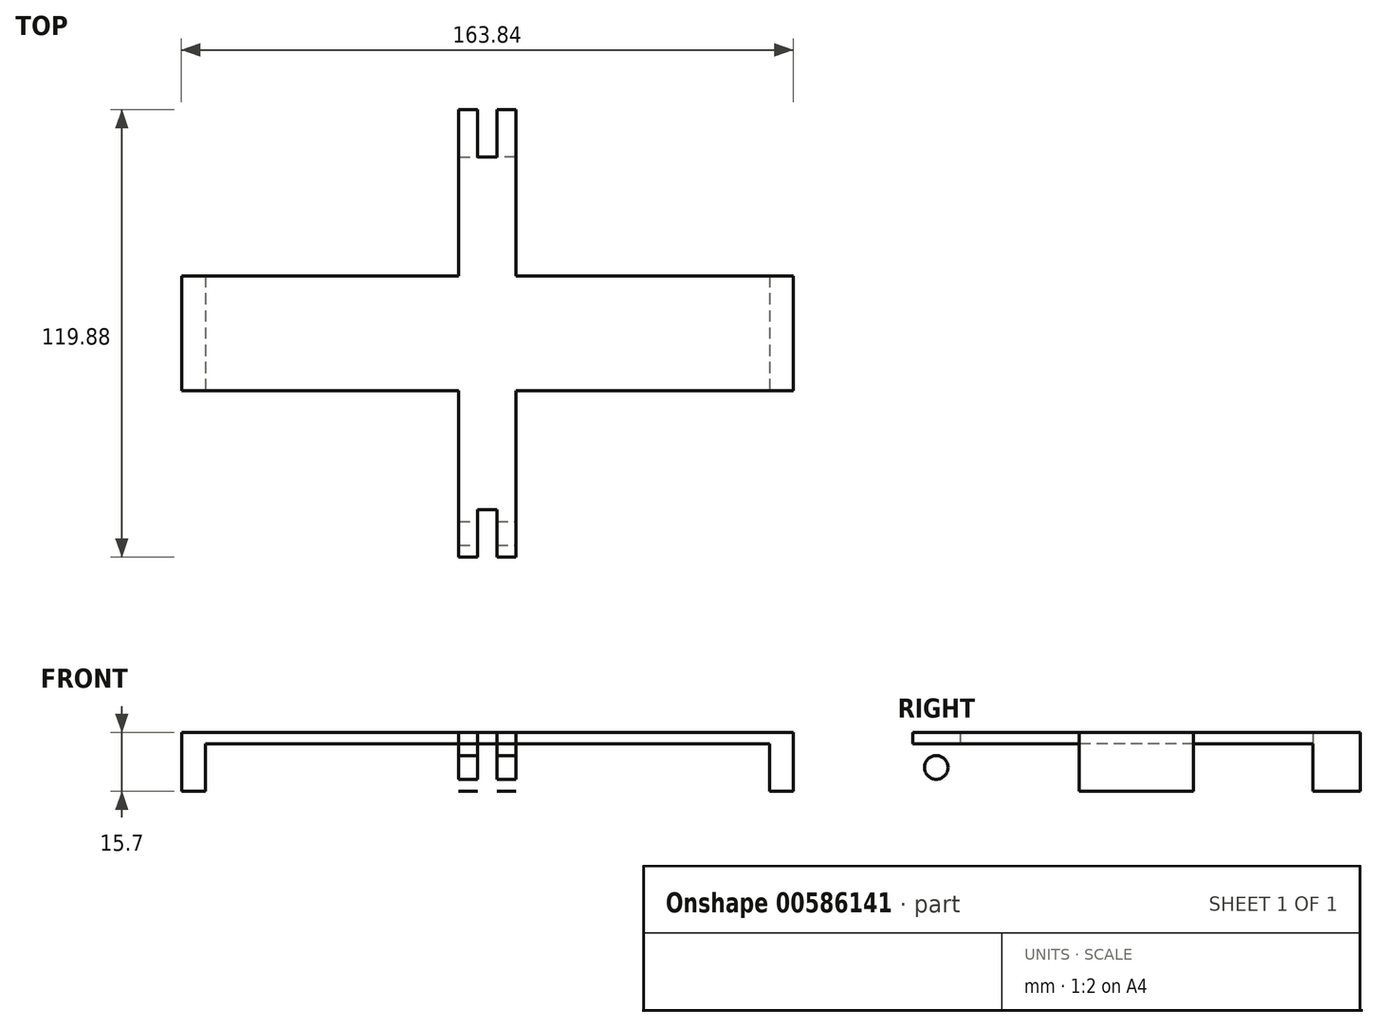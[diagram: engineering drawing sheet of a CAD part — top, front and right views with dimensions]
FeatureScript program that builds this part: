
annotation { "Feature Type Name" : "Feature", "Feature Type Description" : "" }
export const myFeature = defineFeature(function(context is Context, id is Id, definition is map)
    precondition{}
    {
        {
            var Q0;
            Q0=qCreatedBy(makeId("Top.planeOp"),FACE);
            var sketch = newSketch(context, id + "F0", { "sketchPlane" : qUnion([Q0])});
            skLineSegment(sketch, "E0.bottom", {"start": v(-7.62, 59.94) * mm, "end": v(7.62, 59.94) * mm});
            skLineSegment(sketch, "E0.top", {"start": v(-7.62, -59.94) * mm, "end": v(7.62, -59.94) * mm});
            skLineSegment(sketch, "E0.left", {"start": v(-7.62, 59.94) * mm, "end": v(-7.62, 15.36) * mm});
            skLineSegment(sketch, "E0.right", {"start": v(7.62, 59.94) * mm, "end": v(7.62, 15.36) * mm});
            skPoint(sketch, "E0.middle", {"position": v(0, 0) * mm});
            skLineSegment(sketch, "E1.bottom", {"start": v(81.92, 15.36) * mm, "end": v(7.62, 15.36) * mm});
            skLineSegment(sketch, "E1.top", {"start": v(81.92, -15.36) * mm, "end": v(7.62, -15.36) * mm});
            skLineSegment(sketch, "E1.left", {"start": v(81.92, 15.36) * mm, "end": v(81.92, -15.36) * mm});
            skLineSegment(sketch, "E1.right", {"start": v(-81.92, 15.36) * mm, "end": v(-81.92, -15.36) * mm});
            skLineSegment(sketch, "E2.trimOffspring", {"start": v(-7.62, 15.36) * mm, "end": v(-81.92, 15.36) * mm});
            skLineSegment(sketch, "E3.trimOffspring", {"start": v(-7.62, -15.36) * mm, "end": v(-7.62, -59.94) * mm});
            skLineSegment(sketch, "E4.trimOffspring", {"start": v(7.62, -15.36) * mm, "end": v(7.62, -59.94) * mm});
            skLineSegment(sketch, "E5.trimOffspring", {"start": v(-7.62, -15.36) * mm, "end": v(-81.92, -15.36) * mm});
            skPoint(sketch, "E6.endSnap0", {"position": v(0, 59.94) * mm});
            skLineSegment(sketch, "E7", {"start": v(2.88, 59.88) * mm, "end": v(2.88, 59.94) * mm});
            skLineSegment(sketch, "E8", {"start": v(6.35, 53.6) * mm, "end": v(6.35, 59.94) * mm});
            skLineSegment(sketch, "E9.MirrorCS", {"start": v(6.35, -53.6) * mm, "end": v(6.35, -59.94) * mm});
            skLineSegment(sketch, "E10.MirrorCS", {"start": v(2.88, -59.88) * mm, "end": v(2.88, -59.94) * mm});
            skLineSegment(sketch, "E11", {"start": v(-2.54, -53.6) * mm, "end": v(-2.54, -59.94) * mm});
            skPoint(sketch, "E12.orphan", {"position": v(2.88, -59.88) * mm});
            skLineSegment(sketch, "E13", {"start": v(-2.54, 53.6) * mm, "end": v(-2.54, 59.94) * mm});
            skLineSegment(sketch, "E14.bottom", {"start": v(2.54, -47.24) * mm, "end": v(-2.54, -47.24) * mm});
            skLineSegment(sketch, "E14.top", {"start": v(2.54, -59.94) * mm, "end": v(-2.54, -59.94) * mm});
            skLineSegment(sketch, "E14.left", {"start": v(2.54, -47.24) * mm, "end": v(2.54, -59.94) * mm});
            skLineSegment(sketch, "E14.right", {"start": v(-2.54, -47.24) * mm, "end": v(-2.54, -59.94) * mm});
            skPoint(sketch, "E14.middle", {"position": v(0, -53.6) * mm});
            skPoint(sketch, "E14.cornerSnap0", {"position": v(3.8, -47.24) * mm});
            skLineSegment(sketch, "E15.bottom", {"start": v(-2.54, 47.24) * mm, "end": v(2.54, 47.24) * mm});
            skLineSegment(sketch, "E15.top", {"start": v(-2.54, 59.94) * mm, "end": v(2.54, 59.94) * mm});
            skLineSegment(sketch, "E15.left", {"start": v(-2.54, 47.24) * mm, "end": v(-2.54, 59.94) * mm});
            skLineSegment(sketch, "E15.right", {"start": v(2.54, 47.24) * mm, "end": v(2.54, 59.94) * mm});
            skPoint(sketch, "E15.middle", {"position": v(0, 53.6) * mm});
            skPoint(sketch, "E15.cornerSnap0", {"position": v(3.81, 47.24) * mm});
            skSolve(sketch);
        }
        {
            var Q0;
            {var subQ1=sQuery(id+"F0.wireOp",EDGE,"E0.left");Q0=makeQuery(id+"F0.imprint","IMPRINT",FACE,{"disambiguationData":[TD([[makeQuery(id+"F0.imprint","IMPRINT",EDGE,{"derivedFrom":subQ1}),1.0]])]});}
            extrude(context, id + "F1", {"entities" : qUnion([Q0]), "depth" : 3 * mm, "offsetDistance" : 25.4 * mm});
        }
        {
            var Q0;
            Q0=makeQuery(id+"F1.opExtrude","CAP_FACE",FACE,{"disambiguationData":[OSD([sQuery(id+"F0.wireOp",EDGE,"E0.bottom"),sQuery(id+"F0.wireOp",EDGE,"E0.top"),sQuery(id+"F0.wireOp",EDGE,"E0.left"),sQuery(id+"F0.wireOp",EDGE,"E0.right"),sQuery(id+"F0.wireOp",EDGE,"E1.bottom"),sQuery(id+"F0.wireOp",EDGE,"E1.top"),sQuery(id+"F0.wireOp",EDGE,"E1.left"),sQuery(id+"F0.wireOp",EDGE,"E1.right"),sQuery(id+"F0.wireOp",EDGE,"E2.trimOffspring"),sQuery(id+"F0.wireOp",EDGE,"E3.trimOffspring"),sQuery(id+"F0.wireOp",EDGE,"E4.trimOffspring"),sQuery(id+"F0.wireOp",EDGE,"E5.trimOffspring"),sQuery(id+"F0.wireOp",EDGE,"iiGxZXMf-zkiI-TAYv-COHB-aLuBmzG30rmL"),sQuery(id+"F0.wireOp",EDGE,"E7"),sQuery(id+"F0.wireOp",EDGE,"E8"),sQuery(id+"F0.wireOp",EDGE,"257e7fb2-8c07-476a-aaa0-7f0461056c640.MirrorCS"),sQuery(id+"F0.wireOp",EDGE,"E9.MirrorCS"),sQuery(id+"F0.wireOp",EDGE,"E10.MirrorCS")])],"isStart":true});
            var sketch = newSketch(context, id + "F2", { "sketchPlane" : qUnion([Q0])});
            skLineSegment(sketch, "E16.bottom", {"start": v(81.92, -15.36) * mm, "end": v(75.57, -15.36) * mm});
            skLineSegment(sketch, "E16.top", {"start": v(81.92, 15.36) * mm, "end": v(75.57, 15.36) * mm});
            skLineSegment(sketch, "E16.left", {"start": v(81.92, -15.36) * mm, "end": v(81.92, 15.36) * mm});
            skLineSegment(sketch, "E16.right", {"start": v(75.57, -15.36) * mm, "end": v(75.57, 15.36) * mm});
            skLineSegment(sketch, "E17.bottom", {"start": v(7.62, -59.94) * mm, "end": v(2.54, -59.94) * mm});
            skLineSegment(sketch, "E17.top", {"start": v(7.62, -47.24) * mm, "end": v(2.54, -47.24) * mm});
            skLineSegment(sketch, "E17.left", {"start": v(7.62, -59.94) * mm, "end": v(7.62, -47.24) * mm});
            skLineSegment(sketch, "E17.right", {"start": v(2.54, -59.94) * mm, "end": v(2.54, -47.24) * mm});
            skLineSegment(sketch, "E18.MirrorCS", {"start": v(7.62, 47.24) * mm, "end": v(2.54, 47.24) * mm});
            skLineSegment(sketch, "E19.MirrorCS", {"start": v(2.54, 59.94) * mm, "end": v(2.54, 47.24) * mm});
            skLineSegment(sketch, "E20.MirrorCS", {"start": v(7.62, 59.94) * mm, "end": v(2.54, 59.94) * mm});
            skLineSegment(sketch, "E21.MirrorCS", {"start": v(7.62, 59.94) * mm, "end": v(7.62, 47.24) * mm});
            skLineSegment(sketch, "E22.MirrorCS", {"start": v(-2.54, 59.94) * mm, "end": v(-2.54, 47.24) * mm});
            skLineSegment(sketch, "E23.MirrorCS", {"start": v(-7.62, 47.24) * mm, "end": v(-2.54, 47.24) * mm});
            skLineSegment(sketch, "E24.MirrorCS", {"start": v(-7.62, 59.94) * mm, "end": v(-7.62, 47.24) * mm});
            skLineSegment(sketch, "E25.MirrorCS", {"start": v(-7.62, 59.94) * mm, "end": v(-2.54, 59.94) * mm});
            skLineSegment(sketch, "E26.MirrorCS", {"start": v(-7.62, -47.24) * mm, "end": v(-2.54, -47.24) * mm});
            skLineSegment(sketch, "E27.MirrorCS", {"start": v(-7.62, -59.94) * mm, "end": v(-7.62, -47.24) * mm});
            skLineSegment(sketch, "E28.MirrorCS", {"start": v(-2.54, -59.94) * mm, "end": v(-2.54, -47.24) * mm});
            skLineSegment(sketch, "E29.MirrorCS", {"start": v(-7.62, -59.94) * mm, "end": v(-2.54, -59.94) * mm});
            skLineSegment(sketch, "E30.MirrorCS", {"start": v(-75.57, -15.36) * mm, "end": v(-75.57, 15.36) * mm});
            skLineSegment(sketch, "E31.MirrorCS", {"start": v(-81.92, -15.36) * mm, "end": v(-81.92, 15.36) * mm});
            skLineSegment(sketch, "E32.MirrorCS", {"start": v(-81.92, -15.36) * mm, "end": v(-75.57, -15.36) * mm});
            skLineSegment(sketch, "E33.MirrorCS", {"start": v(-81.92, 15.36) * mm, "end": v(-75.57, 15.36) * mm});
            skSolve(sketch);
        }
        {
            var Q0;
            {var subQ0=sQuery(id+"F2.wireOp",EDGE,"E23.MirrorCS");Q0=makeQuery(id+"F2.imprint","IMPRINT",FACE,{"disambiguationData":[TD([[makeQuery(id+"F2.imprint","IMPRINT",EDGE,{"derivedFrom":subQ0}),1.0]])]});}
            var Q1;
            {var subQ3=sQuery(id+"F2.wireOp",EDGE,"E18.MirrorCS");Q1=makeQuery(id+"F2.imprint","IMPRINT",FACE,{"disambiguationData":[TD([[makeQuery(id+"F2.imprint","IMPRINT",EDGE,{"derivedFrom":subQ3}),-1.0]])]});}
            var Q2;
            Q2=makeQuery(id+"F2.imprint","IMPRINT",FACE,{"disambiguationData":[TD([[makeQuery(id+"F2.imprint","IMPRINT",EDGE,{"derivedFrom":sQuery(id+"F2.wireOp",EDGE,"E16.bottom")}),-1.0]])]});
            var Q3;
            {var subQ2=sQuery(id+"F2.wireOp",EDGE,"E17.bottom");Q3=makeQuery(id+"F2.imprint","IMPRINT",FACE,{"disambiguationData":[TD([[makeQuery(id+"F2.imprint","IMPRINT",EDGE,{"derivedFrom":subQ2}),1.0]])]});}
            var Q4;
            {var subQ1=sQuery(id+"F2.wireOp",EDGE,"E26.MirrorCS");Q4=makeQuery(id+"F2.imprint","IMPRINT",FACE,{"disambiguationData":[TD([[makeQuery(id+"F2.imprint","IMPRINT",EDGE,{"derivedFrom":subQ1}),-1.0]])]});}
            var Q5;
            Q5=makeQuery(id+"F2.imprint","IMPRINT",FACE,{"disambiguationData":[TD([[makeQuery(id+"F2.imprint","IMPRINT",EDGE,{"derivedFrom":sQuery(id+"F2.wireOp",EDGE,"E30.MirrorCS")}),1.0]])]});
            extrude(context, id + "F3", {"entities" : qUnion([Q0, Q1, Q2, Q3, Q4, Q5]), "operationType" : NewBodyOperationType.ADD, "depth" : 12.7 * mm, "offsetDistance" : 25.4 * mm});
        }
        {
            var Q0;
            Q0=makeQuery(id+"F3.boolean.opBoolean","MERGE",FACE,{"derivedFrom":[makeQuery(id+"F1.opExtrude","SWEPT_FACE",FACE,{"disambiguationData":[OSD([sQuery(id+"F0.wireOp",EDGE,"E4.trimOffspring")])]}),makeQuery(id+"F3.opExtrude","SWEPT_FACE",FACE,{"disambiguationData":[OSD([sQuery(id+"F2.wireOp",EDGE,"E21.MirrorCS")])]})]});
            var sketch = newSketch(context, id + "F4", { "sketchPlane" : qUnion([Q0])});
            skLineSegment(sketch, "E34.bottom", {"start": v(-59.94, -12.7) * mm, "end": v(-47.24, -12.7) * mm});
            skLineSegment(sketch, "E34.top", {"start": v(-59.94, 0) * mm, "end": v(-47.24, 0) * mm});
            skLineSegment(sketch, "E34.left", {"start": v(-59.94, -12.7) * mm, "end": v(-59.94, 0) * mm});
            skLineSegment(sketch, "E34.right", {"start": v(-47.24, -12.7) * mm, "end": v(-47.24, 0) * mm});
            skLineSegment(sketch, "E35", {"start": v(-59.94, 0) * mm, "end": v(-47.24, -12.7) * mm});
            skCircle(sketch, "E36", {"center": v(-53.6, -6.35) * mm, "radius": 3.18 * mm});
            skCircle(sketch, "E37.MirrorC", {"center": v(53.6, -6.35) * mm, "radius": 3.18 * mm});
            skSolve(sketch);
        }
        {
            var Q0;
            Q0=makeQuery(id+"F4.imprint","IMPRINT",FACE,{"disambiguationData":[TD([[makeQuery(id+"F4.imprint","IMPRINT",EDGE,{"derivedFrom":sQuery(id+"F4.wireOp",EDGE,"E37.MirrorC")}),-1.0]])]});
            var Q1;
            {var subQ0=sQuery(id+"F4.wireOp",EDGE,"E36");var subQ1=sQuery(id+"F4.wireOp",EDGE,"E35");var subQ2=makeQuery(id+"F4.imprint","INTERSECT",VERTEX,{"disambiguationData":[OD(0.0)],"derivedFrom":[subQ1,subQ0]});Q1=makeQuery(id+"F4.imprint","IMPRINT",FACE,{"disambiguationData":[TD([[makeQuery(id+"F4.imprint","IMPRINT",EDGE,{"disambiguationData":[TD([[subQ2,-1.0]])],"derivedFrom":subQ1}),1.0]])]});}
            var Q2;
            {var subQ0=sQuery(id+"F4.wireOp",EDGE,"E36");var subQ1=sQuery(id+"F4.wireOp",EDGE,"E35");var subQ2=makeQuery(id+"F4.imprint","INTERSECT",VERTEX,{"disambiguationData":[OD(0.0)],"derivedFrom":[subQ1,subQ0]});Q2=makeQuery(id+"F4.imprint","IMPRINT",FACE,{"disambiguationData":[TD([[makeQuery(id+"F4.imprint","IMPRINT",EDGE,{"disambiguationData":[TD([[subQ2,-1.0]])],"derivedFrom":subQ1}),-1.0]])]});}
            extrude(context, id + "F5", {"entities" : qUnion([Q0, Q1, Q2]), "operationType" : NewBodyOperationType.REMOVE, "oppositeDirection" : true, "depth" : 25.4 * mm, "offsetDistance" : 25.4 * mm});
        }
    });
